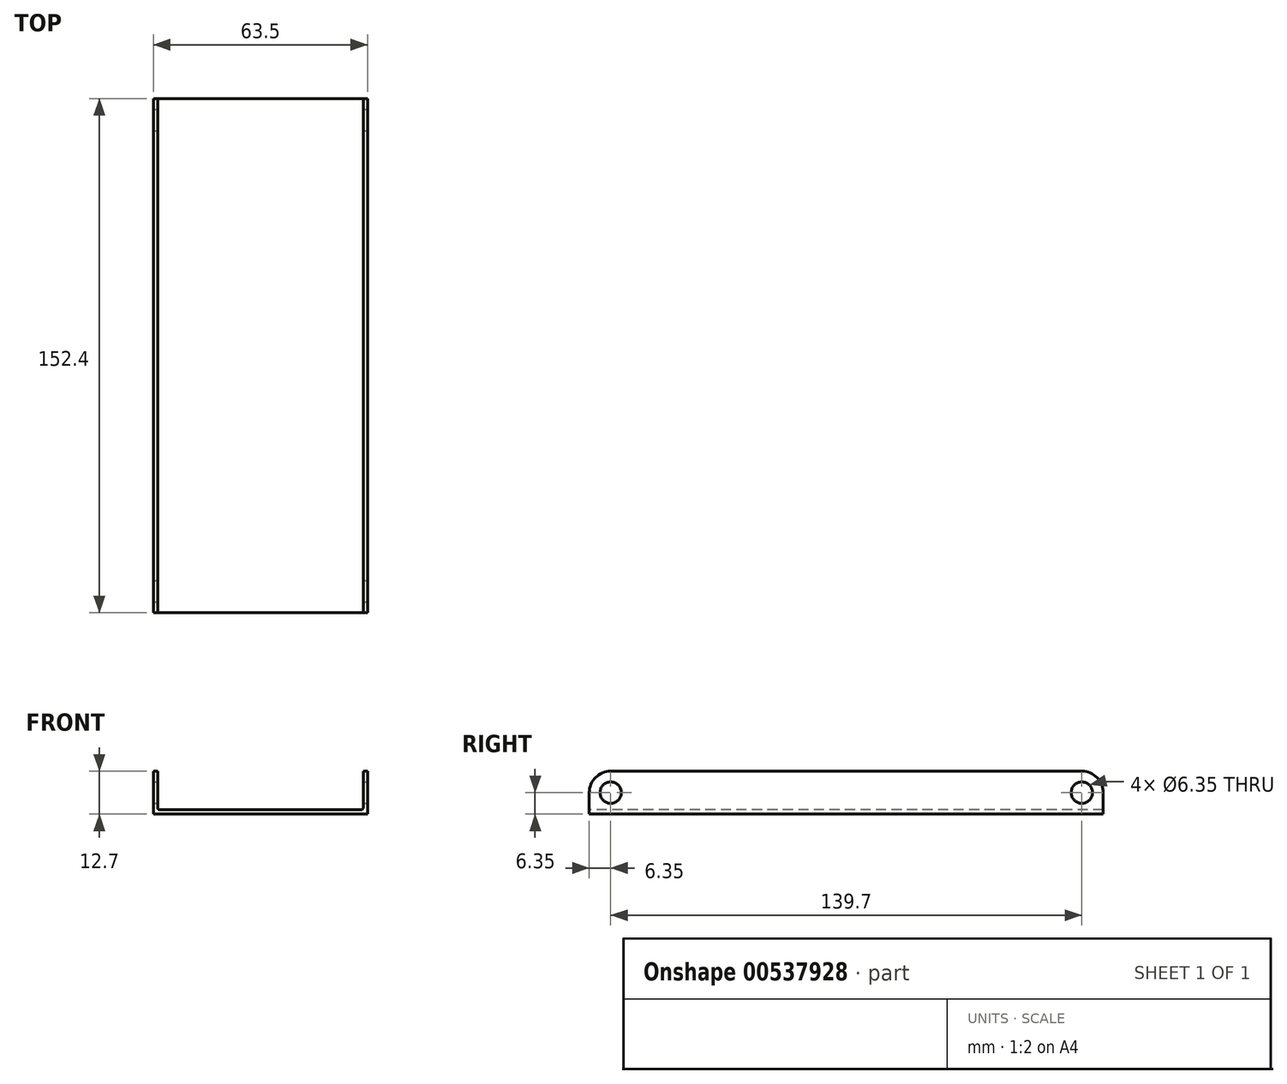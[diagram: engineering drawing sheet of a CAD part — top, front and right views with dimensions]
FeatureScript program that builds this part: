
annotation { "Feature Type Name" : "Feature", "Feature Type Description" : "" }
export const myFeature = defineFeature(function(context is Context, id is Id, definition is map)
    precondition{}
    {
        {
            var Q0;
            Q0=qCreatedBy(makeId("Front.planeOp"),FACE);
            var sketch = newSketch(context, id + "F0", { "sketchPlane" : qUnion([Q0])});
            skLineSegment(sketch, "E0", {"start": v(0, 0) * mm, "end": v(-63.5, 0) * mm});
            skLineSegment(sketch, "E1", {"start": v(-63.5, 0) * mm, "end": v(-63.5, 12.7) * mm});
            skLineSegment(sketch, "E2", {"start": v(-63.5, 12.7) * mm, "end": v(-62.23, 12.7) * mm});
            skLineSegment(sketch, "E3", {"start": v(-62.23, 12.7) * mm, "end": v(-62.23, 1.9) * mm});
            skLineSegment(sketch, "E4", {"start": v(-61.6, 1.27) * mm, "end": v(-1.9, 1.27) * mm});
            skLineSegment(sketch, "E5", {"start": v(-1.27, 1.9) * mm, "end": v(-1.27, 12.7) * mm});
            skLineSegment(sketch, "E6", {"start": v(-1.27, 12.7) * mm, "end": v(0, 12.7) * mm});
            skLineSegment(sketch, "E7", {"start": v(0, 12.7) * mm, "end": v(0, 0) * mm});
            skPoint(sketch, "E8.visualSharp", {"position": v(-62.23, 1.27) * mm});
            skArc(sketch, "E8.filletArc", {"start": v(-62.23, 1.9) * mm, "mid": v(-62.04, 1.46) * mm, "end": v(-61.6, 1.27) * mm});
            skPoint(sketch, "E9.visualSharp", {"position": v(-1.27, 1.27) * mm});
            skArc(sketch, "E9.filletArc", {"start": v(-1.9, 1.27) * mm, "mid": v(-1.46, 1.46) * mm, "end": v(-1.27, 1.9) * mm});
            skSolve(sketch);
        }
        {
            var Q0;
            Q0 = qSketchRegion(id + "F0", true);
            extrude(context, id + "F1", {"entities" : qUnion([Q0]), "oppositeDirection" : true, "depth" : 152.4 * mm, "offsetDistance" : 25.4 * mm});
        }
        {
            var Q0;
            Q0=makeQuery(id+"F1.opExtrude","SWEPT_FACE",FACE,{"disambiguationData":[OSD([sQuery(id+"F0.wireOp",EDGE,"E7")])]});
            var sketch = newSketch(context, id + "F2", { "sketchPlane" : qUnion([Q0])});
            skCircle(sketch, "E10", {"center": v(6.35, 6.35) * mm, "radius": 3.18 * mm});
            skLineSegment(sketch, "E11", {"start": v(6.35, 12.7) * mm, "end": v(6.35, 12.7) * mm});
            skLineSegment(sketch, "E12", {"start": v(0, 6.35) * mm, "end": v(0, 6.35) * mm});
            skPoint(sketch, "E13.visualSharp", {"position": v(0, 12.7) * mm});
            skArc(sketch, "E13.filletArc", {"start": v(6.35, 12.7) * mm, "mid": v(1.86, 10.84) * mm, "end": v(0, 6.35) * mm});
            skLineSegment(sketch, "E14", {"start": v(0, 12.7) * mm, "end": v(6.35, 12.7) * mm});
            skLineSegment(sketch, "E15", {"start": v(0, 12.7) * mm, "end": v(0, 6.35) * mm});
            skLineSegment(sketch, "E16", {"start": v(76.2, 12.7) * mm, "end": v(76.2, 0) * mm, "construction": true});
            skArc(sketch, "E17.MirrorCS", {"start": v(146.05, 12.7) * mm, "mid": v(150.54, 10.84) * mm, "end": v(152.4, 6.35) * mm});
            skCircle(sketch, "E18.MirrorC", {"center": v(146.05, 6.35) * mm, "radius": 3.18 * mm});
            skLineSegment(sketch, "E19.MirrorCS", {"start": v(152.4, 12.7) * mm, "end": v(146.05, 12.7) * mm});
            skLineSegment(sketch, "E20.MirrorCS", {"start": v(152.4, 12.7) * mm, "end": v(152.4, 6.35) * mm});
            skSolve(sketch);
        }
        {
            var Q0;
            Q0 = qSketchRegion(id + "F2", true);
            extrude(context, id + "F3", {"entities" : qUnion([Q0]), "operationType" : NewBodyOperationType.REMOVE, "endBound" : BoundingType.THROUGH_ALL, "oppositeDirection" : true, "depth" : 25.4 * mm, "offsetDistance" : 25.4 * mm});
        }
    });
